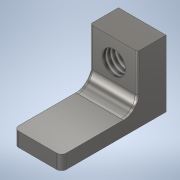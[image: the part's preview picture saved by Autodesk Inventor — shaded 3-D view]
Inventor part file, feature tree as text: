
AUTODESK INVENTOR PART (.ipt)
format: ipt  version: 2020 (Build 240168000, 168)  size: 323,584 bytes
history: native  units: mm
features: fillet x3, sketch x3, projected_geometry x2, extrude x1, hole x1, chamfer x1
ambient origin geometry x8: Origin, YZ Plane, XZ Plane, XY Plane, X Axis, Y Axis, Z Axis, Center Point
bodies: Volumenkörper1 (feature_tree)
feature tree (11):
  extrude  "Extrusion1"  Depth=6.0mm
  hole  "Bohrung1"  [1 undecoded]
  chamfer  "Fase1"  Distance=10.0mm
  fillet  "Rundung1"  Radius=2.0mm
  fillet  "Rundung2"  Radius=0.5mm
  sketch  "Skizze5"  dims[d7=4.917mm d8=12.0mm d9=4.0mm d10=2.0mm d11=90.0deg d12=17.1mm d13=20.594885mm d14=2.0mm d15=2.0mm d16=45.0deg d38=0.5mm d39=1.0mm d40=3.0mm]
  fillet  "Fillet3"  Radius=1.0mm
  sketch  "Skizze1"  dims[d0=14.0mm d1=6.0mm]
  sketch  "Skizze2"  dims[d2=3.0mm d3=22.0mm d4=10.0mm d5=0.0mm]
  projected_geometry  "Projizierte Kontur1"
  projected_geometry  "Projizierte Kontur4"
note: 1 required parameter value undecoded (feature->parameter linkage not recoverable at this tier; creation-order binding heuristic only, values carry confidence <= 0.55)
